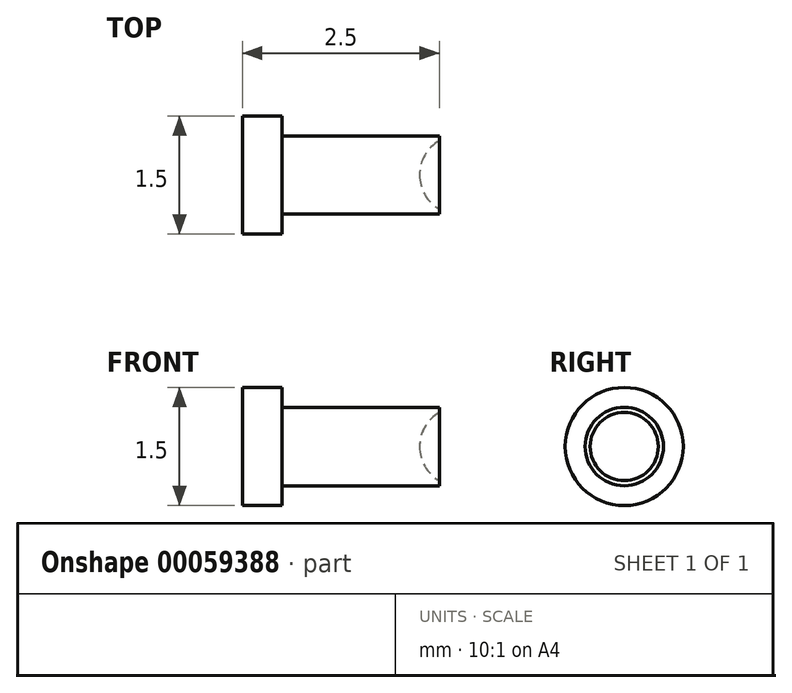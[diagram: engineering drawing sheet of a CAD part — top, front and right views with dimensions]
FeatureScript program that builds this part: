
annotation { "Feature Type Name" : "Feature", "Feature Type Description" : "" }
export const myFeature = defineFeature(function(context is Context, id is Id, definition is map)
    precondition{}
    {
        {
            var Q0;
            Q0=qCreatedBy(makeId("Front.planeOp"),FACE);
            var sketch = newSketch(context, id + "F0", { "sketchPlane" : qUnion([Q0])});
            skLineSegment(sketch, "E0.bottom", {"start": v(0, 0) * mm, "end": v(0.5, 0) * mm});
            skLineSegment(sketch, "E0.top", {"start": v(0, 0.75) * mm, "end": v(0.5, 0.75) * mm});
            skLineSegment(sketch, "E0.left", {"start": v(0, 0) * mm, "end": v(0, 0.75) * mm});
            skLineSegment(sketch, "E0.right", {"start": v(0.5, 0) * mm, "end": v(0.5, 0.75) * mm});
            skLineSegment(sketch, "E1.bottom", {"start": v(0.5, 0) * mm, "end": v(2.5, 0) * mm});
            skLineSegment(sketch, "E1.top", {"start": v(0.5, 0.5) * mm, "end": v(2.5, 0.5) * mm});
            skLineSegment(sketch, "E1.left", {"start": v(0.5, 0) * mm, "end": v(0.5, 0.5) * mm});
            skLineSegment(sketch, "E1.right", {"start": v(2.5, 0) * mm, "end": v(2.5, 0.5) * mm});
            skArc(sketch, "E2", {"start": v(2.5, 0.43) * mm, "mid": v(2.32, 0.25) * mm, "end": v(2.25, 0) * mm});
            skSolve(sketch);
        }
        {
            var Q0;
            Q0=makeQuery(id+"F0.imprint","IMPRINT",FACE,{"disambiguationData":[TD([[makeQuery(id+"F0.imprint","IMPRINT",EDGE,{"derivedFrom":sQuery(id+"F0.wireOp",EDGE,"E0.bottom")}),1.0]])]});
            var Q1;
            {var subQ1=sQuery(id+"F0.wireOp",EDGE,"E1.top");Q1=makeQuery(id+"F0.imprint","IMPRINT",FACE,{"disambiguationData":[TD([[makeQuery(id+"F0.imprint","IMPRINT",EDGE,{"derivedFrom":subQ1}),-1.0]])]});}
            var Q2;
            Q2=sQuery(id+"F0.wireOp",EDGE,"E1.bottom");
            revolve(context, id + "F1", {"entities" : qUnion([Q0, Q1]), "axis" : qUnion([Q2]), "revolveType" : RevolveType.FULL});
        }
    });
